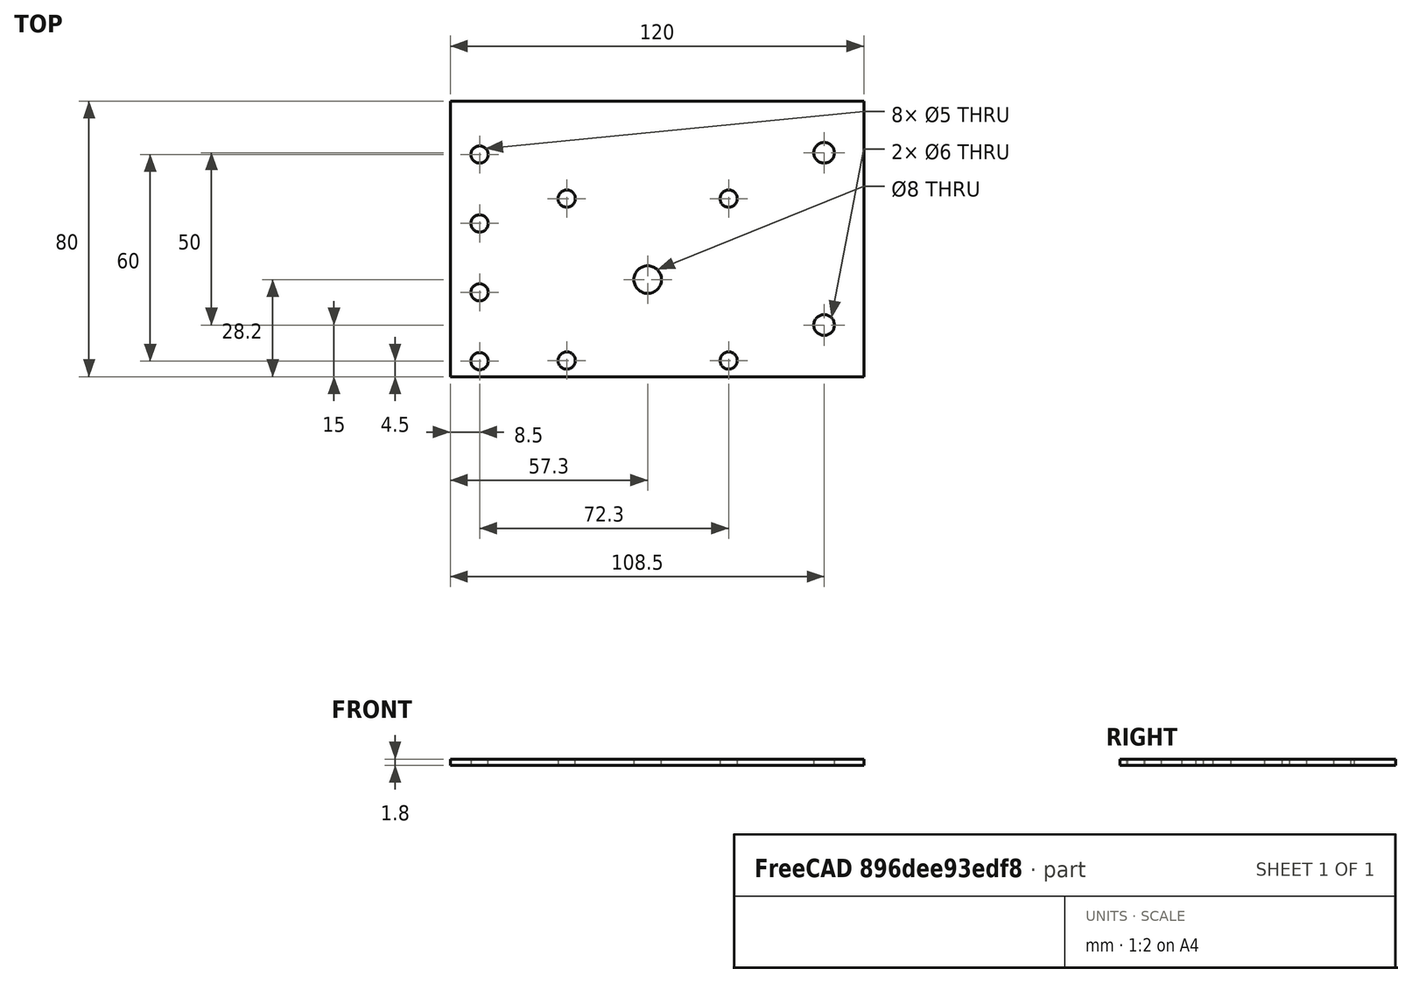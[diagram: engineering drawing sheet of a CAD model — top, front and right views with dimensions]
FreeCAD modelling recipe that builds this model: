
FCSTD DOCUMENT  (FreeCAD 0.19R24276 (Git))
Label: Bar_80x120__1_8mm_Nema23_support
License: All rights reserved
LicenseURL: http://en.wikipedia.org/wiki/All_rights_reserved
objects: Sketcher::SketchObject×1, PartDesign::Pad×1, PartDesign::Body×1
note: 4 computed .brp shape members not serialized (recipe doc carries the construction recipe); baked Part::Feature solids carry a one-line shape summary decoded from their .brp

FEATURE [Sketcher::SketchObject] Sketch
  FullyConstrained = false
  MapMode = 5
  Support = -> [XY_Plane]
  sketch-geometry (69):
    g0: LineSegment StartX=0 StartY=0 StartZ=0 EndX=120 EndY=0 EndZ=0
    g1: LineSegment StartX=120 StartY=0 StartZ=0 EndX=120 EndY=80 EndZ=0
    g2: LineSegment StartX=120 StartY=80 StartZ=0 EndX=0 EndY=80 EndZ=0
    g3: LineSegment StartX=0 StartY=80 StartZ=0 EndX=0 EndY=0 EndZ=0
    g4: LineSegment StartX=0 StartY=4.5 StartZ=0 EndX=120 EndY=4.5 EndZ=0
    g5: LineSegment StartX=0 StartY=24.5 StartZ=0 EndX=120 EndY=24.5 EndZ=0
    g6: LineSegment StartX=0 StartY=44.5 StartZ=0 EndX=120 EndY=44.5 EndZ=0
    g7: LineSegment StartX=0 StartY=64.5 StartZ=0 EndX=120 EndY=64.5 EndZ=0
    g8: LineSegment StartX=48.5 StartY=0 StartZ=0 EndX=48.5 EndY=4.5 EndZ=0
    g9: LineSegment StartX=68.5 StartY=0 StartZ=0 EndX=68.5 EndY=4.5 EndZ=0
    g10: LineSegment StartX=88.5 StartY=0 StartZ=0 EndX=88.5 EndY=4.5 EndZ=0
    g11: LineSegment StartX=108.5 StartY=0 StartZ=0 EndX=108.5 EndY=4.5 EndZ=0
    g12: LineSegment StartX=0 StartY=14.5 StartZ=0 EndX=120 EndY=14.5 EndZ=0
    g13: LineSegment StartX=0 StartY=34.5 StartZ=0 EndX=120 EndY=34.5 EndZ=0
    g14: LineSegment StartX=0 StartY=54.5 StartZ=0 EndX=120 EndY=54.5 EndZ=0
    g15: LineSegment StartX=0 StartY=74.5 StartZ=0 EndX=120 EndY=74.5 EndZ=0
    g16: LineSegment StartX=48.5 StartY=24.5 StartZ=0 EndX=48.5 EndY=80 EndZ=0
    g17: LineSegment StartX=68.5 StartY=14.5 StartZ=0 EndX=68.5 EndY=80 EndZ=0
    g18: LineSegment StartX=88.5 StartY=24.5 StartZ=0 EndX=88.5 EndY=80 EndZ=0
    g19: LineSegment StartX=108.5 StartY=14.5 StartZ=0 EndX=108.5 EndY=80 EndZ=0
    g20: Circle CenterX=8.5 CenterY=4.5 CenterZ=0 NormalX=0 NormalY=0 NormalZ=1 AngleXU=0 Radius=2.5
    g21: Circle CenterX=48.5 CenterY=4.5 CenterZ=0 NormalX=0 NormalY=0 NormalZ=1 AngleXU=0 Radius=2.5
    g22: Circle CenterX=88.5 CenterY=4.5 CenterZ=0 NormalX=0 NormalY=0 NormalZ=1 AngleXU=0 Radius=2.5
    g23: Circle CenterX=28.5 CenterY=14.5 CenterZ=0 NormalX=0 NormalY=0 NormalZ=1 AngleXU=0 Radius=2.5
    g24: Circle CenterX=108.5 CenterY=14.5 CenterZ=0 NormalX=0 NormalY=0 NormalZ=1 AngleXU=0 Radius=2.5
    g25: Circle CenterX=8.5 CenterY=24.5 CenterZ=0 NormalX=0 NormalY=0 NormalZ=1 AngleXU=0 Radius=2.5
    g26: Circle CenterX=48.5 CenterY=24.5 CenterZ=0 NormalX=0 NormalY=0 NormalZ=1 AngleXU=0 Radius=2.5
    g27: Circle CenterX=88.5 CenterY=24.5 CenterZ=0 NormalX=0 NormalY=0 NormalZ=1 AngleXU=0 Radius=2.5
    g28: Circle CenterX=8.5 CenterY=44.5 CenterZ=0 NormalX=0 NormalY=0 NormalZ=1 AngleXU=0 Radius=2.5
    g29: Circle CenterX=48.5 CenterY=44.5 CenterZ=0 NormalX=0 NormalY=0 NormalZ=1 AngleXU=0 Radius=2.5
    g30: Circle CenterX=88.5 CenterY=44.5 CenterZ=0 NormalX=0 NormalY=0 NormalZ=1 AngleXU=0 Radius=2.5
    g31: Circle CenterX=28.5 CenterY=54.5 CenterZ=0 NormalX=0 NormalY=0 NormalZ=1 AngleXU=0 Radius=2.5
    g32: Circle CenterX=68.5 CenterY=54.5 CenterZ=0 NormalX=0 NormalY=0 NormalZ=1 AngleXU=0 Radius=2.5
    g33: Circle CenterX=108.5 CenterY=54.5 CenterZ=0 NormalX=0 NormalY=0 NormalZ=1 AngleXU=0 Radius=2.5
    g34: Circle CenterX=88.5 CenterY=64.5 CenterZ=0 NormalX=0 NormalY=0 NormalZ=1 AngleXU=0 Radius=2.5
    g35: Circle CenterX=48.5 CenterY=64.5 CenterZ=0 NormalX=0 NormalY=0 NormalZ=1 AngleXU=0 Radius=2.5
    g36: Circle CenterX=8.5 CenterY=64.5 CenterZ=0 NormalX=0 NormalY=0 NormalZ=1 AngleXU=0 Radius=2.5
    g37: Circle CenterX=28.5 CenterY=34.5 CenterZ=0 NormalX=0 NormalY=0 NormalZ=1 AngleXU=0 Radius=2.5
    g38: Circle CenterX=68.5 CenterY=34.5 CenterZ=0 NormalX=0 NormalY=0 NormalZ=1 AngleXU=0 Radius=2.5
    g39: Circle CenterX=108.5 CenterY=34.5 CenterZ=0 NormalX=0 NormalY=0 NormalZ=1 AngleXU=0 Radius=2.5
    g40: Circle CenterX=28.5 CenterY=74.5 CenterZ=0 NormalX=0 NormalY=0 NormalZ=1 AngleXU=0 Radius=2.5
    g41: Circle CenterX=68.5 CenterY=74.5 CenterZ=0 NormalX=0 NormalY=0 NormalZ=1 AngleXU=0 Radius=2.5
    g42: Circle CenterX=108.5 CenterY=74.5 CenterZ=0 NormalX=0 NormalY=0 NormalZ=1 AngleXU=0 Radius=2.5
    g43: LineSegment StartX=28.5 StartY=74.5 StartZ=0 EndX=28.5 EndY=14.5 EndZ=0
    g44: LineSegment StartX=8.5 StartY=4.5 StartZ=0 EndX=8.5 EndY=24.5 EndZ=0
    g45: Circle CenterX=68.5 CenterY=14.5 CenterZ=0 NormalX=0 NormalY=0 NormalZ=1 AngleXU=0 Radius=2.5
    g46: LineSegment StartX=57.3 StartY=0 StartZ=0 EndX=57.3 EndY=80 EndZ=0
    g47: LineSegment StartX=85.5 StartY=80 StartZ=0 EndX=85.5 EndY=0 EndZ=0
    g48: LineSegment StartX=0 StartY=28.2 StartZ=0 EndX=57.3 EndY=28.2 EndZ=0
    g49: LineSegment StartX=85.5 StartY=28.2 StartZ=0 EndX=120 EndY=28.2 EndZ=0
    g50: LineSegment StartX=80.8 StartY=51.7 StartZ=0 EndX=33.8 EndY=51.7 EndZ=0
    g51: LineSegment StartX=33.8 StartY=51.7 StartZ=0 EndX=33.8 EndY=4.7 EndZ=0
    g52: LineSegment StartX=33.8 StartY=4.7 StartZ=0 EndX=80.8 EndY=4.7 EndZ=0
    g53: LineSegment StartX=80.8 StartY=4.7 StartZ=0 EndX=80.8 EndY=51.7 EndZ=0
    g54: Circle CenterX=57.3 CenterY=28.2 CenterZ=0 NormalX=0 NormalY=0 NormalZ=1 AngleXU=0 Radius=33.234
    g55: LineSegment StartX=85.5 StartY=56.4 StartZ=0 EndX=29.1 EndY=56.4 EndZ=0
    g56: LineSegment StartX=29.1 StartY=56.4 StartZ=0 EndX=29.1 EndY=0 EndZ=0
    g57: LineSegment StartX=29.1 StartY=-1.9e-15 StartZ=0 EndX=85.5 EndY=-1e-16 EndZ=0
    g58: LineSegment StartX=85.5 StartY=-1e-16 StartZ=0 EndX=85.5 EndY=56.4 EndZ=0
    g59: Circle CenterX=57.3 CenterY=28.2 CenterZ=0 NormalX=0 NormalY=0 NormalZ=1 AngleXU=0 Radius=39.8808
    g60: Circle CenterX=33.8 CenterY=51.7 CenterZ=0 NormalX=0 NormalY=0 NormalZ=1 AngleXU=0 Radius=2.5
    g61: Circle CenterX=80.8 CenterY=51.7 CenterZ=0 NormalX=0 NormalY=0 NormalZ=1 AngleXU=0 Radius=2.5
    g62: Circle CenterX=33.8 CenterY=4.7 CenterZ=0 NormalX=0 NormalY=0 NormalZ=1 AngleXU=0 Radius=2.5
    g63: Circle CenterX=80.8 CenterY=4.7 CenterZ=0 NormalX=0 NormalY=0 NormalZ=1 AngleXU=0 Radius=2.5
    g64: Circle CenterX=57.3 CenterY=28.2 CenterZ=0 NormalX=0 NormalY=0 NormalZ=1 AngleXU=0 Radius=4
    g65: LineSegment StartX=100.727 StartY=15 StartZ=0 EndX=106.051 EndY=15 EndZ=0
    g66: LineSegment StartX=108.5 StartY=15 StartZ=0 EndX=120 EndY=15 EndZ=0
    g67: Circle CenterX=108.5 CenterY=15 CenterZ=0 NormalX=0 NormalY=0 NormalZ=1 AngleXU=0 Radius=3
    g68: Circle CenterX=108.5 CenterY=65 CenterZ=0 NormalX=0 NormalY=0 NormalZ=1 AngleXU=0 Radius=3
  constraints (207):
    c: Coincident(g0,g1)
    c: Coincident(g1,g2)
    c: Coincident(g2,g3)
    c: Coincident(g3,g0)
    c: Horizontal(g0)
    c: Horizontal(g2)
    c: Vertical(g1)
    c: Vertical(g3)
    c: Coincident(g0,g-1)
    c: DistanceX(g0,g0) = 120
    c: DistanceY(g3,g3) = 80
    c: Horizontal(g4)
    c: PointOnObject(g4,g3)
    c: PointOnObject(g4,g1)
    c: Horizontal(g5)
    c: PointOnObject(g5,g3)
    c: PointOnObject(g5,g1)
    c: DistanceY(g4,g5) = 20
    c: Horizontal(g6)
    c: PointOnObject(g6,g1)
    c: PointOnObject(g6,g3)
    c: DistanceY(g5,g6) = 20
    c: Horizontal(g7)
    c: PointOnObject(g7,g1)
    c: PointOnObject(g7,g3)
    c: DistanceY(g6,g7) = 20
    c: Vertical(g8)
    c: Vertical(g9)
    c: Vertical(g10)
    c: Vertical(g11)
    c: PointOnObject(g8,g0)
    c: PointOnObject(g9,g0)
    c: PointOnObject(g10,g0)
    c: PointOnObject(g11,g0)
    c: PointOnObject(g19,g2)
    c: PointOnObject(g18,g2)
    c: PointOnObject(g17,g2)
    c: PointOnObject(g16,g2)
    c: DistanceX(g8,g9) = 20
    c: DistanceX(g9,g10) = 20
    c: DistanceX(g10,g11) = 20
    c: Horizontal(g12)
    c: Horizontal(g13)
    c: Horizontal(g14)
    c: Horizontal(g15)
    c: PointOnObject(g12,g3)
    c: PointOnObject(g13,g3)
    c: PointOnObject(g14,g3)
    c: PointOnObject(g15,g3)
    c: PointOnObject(g15,g1)
    c: PointOnObject(g14,g1)
    c: PointOnObject(g13,g1)
    c: PointOnObject(g12,g1)
    c: DistanceY(g0,g12) = 14.5
    c: DistanceY(g12,g13) = 20
    c: DistanceY(g13,g14) = 20
    c: DistanceY(g14,g15) = 20
    c: PointOnObject(g20,g4)
    c: PointOnObject(g23,g12)
    c: PointOnObject(g8,g4)
    c: Tangent(g8,g16)
    c: PointOnObject(g9,g4)
    c: PointOnObject(g17,g12)
    c: Tangent(g9,g17)
    c: PointOnObject(g10,g4)
    c: Tangent(g10,g18)
    c: PointOnObject(g11,g4)
    c: PointOnObject(g19,g12)
    c: Tangent(g11,g19)
    c: Coincident(g21,g8)
    c: Coincident(g22,g10)
    c: Coincident(g24,g19)
    c: Equal(g20,g23)
    c: Equal(g23,g21)
    c: Equal(g21,g22)
    c: Equal(g22,g24)
    c: Diameter(g23) = 5
    c: PointOnObject(g16,g5)
    c: PointOnObject(g18,g5)
    c: Equal(g26,g27)
    c: Equal(g36,g31)
    c: Equal(g31,g35)
    c: Equal(g35,g34)
    c: Equal(g34,g33)
    c: Diameter(g31) = 5
    c: Equal(g34,g32)
    c: Equal(g29,g30)
    c: Diameter(g37) = 5
    c: Diameter(g40) = 5
    c: Coincident(g43,g40)
    c: Coincident(g43,g23)
    c: Vertical(g43)
    c: DistanceX(g20,g23) = 20
    c: DistanceX(g0,g20) = 8.5
    c: DistanceY(g0,g4) = 4.5
    c: Coincident(g44,g20)
    c: Coincident(g44,g25)
    c: Vertical(g44)
    c: Coincident(g45,g17)
    c: Equal(g24,g45)
    c: Vertical(g24,g39)
    c: Vertical(g39,g33)
    c: Vertical(g33,g42)
    c: Vertical(g34,g30)
    c: Vertical(g30,g27)
    c: Vertical(g27,g22)
    c: Vertical(g41,g32)
    c: Vertical(g32,g38)
    c: Vertical(g38,g45)
    c: Vertical(g21,g26)
    c: Vertical(g26,g29)
    c: Vertical(g29,g35)
    c: Vertical(g23,g37)
    c: Vertical(g37,g31)
    c: Vertical(g36,g28)
    c: Vertical(g28,g25)
    c: Horizontal(g25,g27)
    c: Horizontal(g27,g26)
    c: DistanceX(g23,g8) = 20
    c: Horizontal(g27,g5)
    c: Equal(g25,g20)
    c: Equal(g27,g25)
    c: Horizontal(g37,g38)
    c: Horizontal(g38,g39)
    c: Horizontal(g39,g13)
    c: Equal(g37,g38)
    c: Equal(g38,g39)
    c: Horizontal(g28,g29)
    c: Horizontal(g29,g30)
    c: Horizontal(g30,g6)
    c: Equal(g28,g29)
    c: Equal(g30,g38)
    c: Horizontal(g31,g32)
    c: Horizontal(g32,g33)
    c: Horizontal(g33,g14)
    c: Horizontal(g36,g35)
    c: Horizontal(g35,g34)
    c: Horizontal(g34,g7)
    c: Horizontal(g40,g41)
    c: Horizontal(g41,g42)
    c: Equal(g40,g41)
    c: Equal(g41,g42)
    c: Horizontal(g42,g15)
    c: Vertical(g46)
    c: PointOnObject(g46,g0)
    c: Vertical(g47)
    c: PointOnObject(g47,g0)
    c: DistanceX(g46,g47) = 28.2
    c: Horizontal(g48)
    c: PointOnObject(g49,g1)
    c: PointOnObject(g47,g2)
    c: PointOnObject(g46,g2)
    c: PointOnObject(g48,g3)
    c: DistanceY(g0,g49) = 28.2
    c: PointOnObject(g49,g47)
    c: Tangent(g48,g49)
    c: PointOnObject(g48,g46)
    c: Coincident(g50,g51)
    c: Coincident(g51,g52)
    c: Coincident(g52,g53)
    c: Coincident(g53,g50)
    c: Equal(g50,g51)
    c: Equal(g50,g52)
    c: Equal(g50,g53)
    c: PointOnObject(g50,g54)
    c: PointOnObject(g51,g54)
    c: PointOnObject(g52,g54)
    c: PointOnObject(g53,g54)
    c: Coincident(g54,g48)
    c: Coincident(g55,g56)
    c: Coincident(g56,g57)
    c: Coincident(g57,g58)
    c: Coincident(g58,g55)
    c: Equal(g55,g56)
    c: Equal(g55,g57)
    c: Equal(g55,g58)
    c: PointOnObject(g55,g59)
    c: PointOnObject(g56,g59)
    c: PointOnObject(g57,g59)
    c: PointOnObject(g58,g59)
    c: Coincident(g59,g48)
    c: Horizontal(g50)
    c: Horizontal(g55)
    c: DistanceX(g57,g57) = 56.4
    c: DistanceX(g52,g52) = 47
    c: Coincident(g60,g50)
    c: Coincident(g61,g50)
    c: Coincident(g62,g51)
    c: Coincident(g63,g52)
    c: Diameter(g62) = 5
    c: Equal(g62,g60)
    c: Equal(g62,g61)
    c: Equal(g62,g63)
    c: Coincident(g64,g48)
    c: Diameter(g64) = 8
    c: DistanceX(g47,g24) = 23
    c: Horizontal(g65)
    c: PointOnObject(g66,g1)
    c: DistanceY(g0,g66) = 15
    c: PointOnObject(g65,g24)
    c: PointOnObject(g66,g19)
    c: Tangent(g65,g66)
    c: Coincident(g67,g66)
    c: Diameter(g67) = 6
    c: Equal(g67,g68)
    c: Vertical(g67,g68)
    c: DistanceY(g67,g68) = 50
FEATURE [PartDesign::Pad] Pad
  Direction = (1,1,1)
  Length = 1.8
  Length2 = 100
  Profile = -> Sketch
  Type = 0
FEATURE [PartDesign::Body] Body
  Group = -> [Sketch,Pad]
  Origin = -> Origin
  Tip = -> Pad
